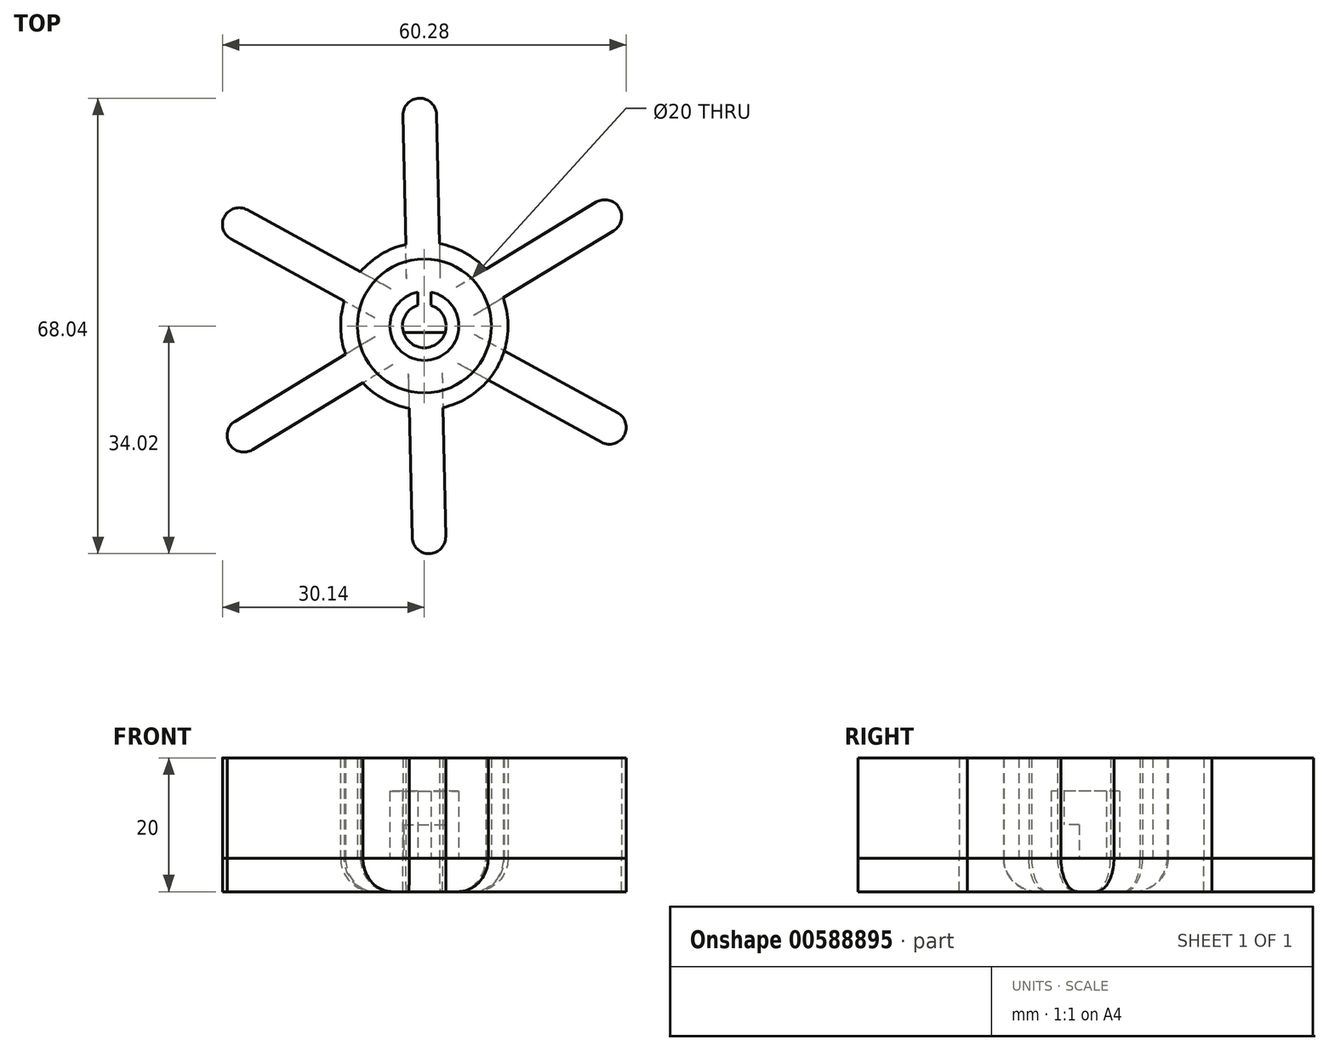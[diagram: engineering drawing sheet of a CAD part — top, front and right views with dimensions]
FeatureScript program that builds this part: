
annotation { "Feature Type Name" : "Feature", "Feature Type Description" : "" }
export const myFeature = defineFeature(function(context is Context, id is Id, definition is map)
    precondition{}
    {
        {
            var Q0;
            Q0=qCreatedBy(makeId("Top.planeOp"),FACE);
            var sketch = newSketch(context, id + "F0", { "sketchPlane" : qUnion([Q0])});
            skArc(sketch, "E0", {"start": v(-1, 3.1) * mm, "mid": v(0, -3.25) * mm, "end": v(1, 3.1) * mm});
            skArc(sketch, "E1", {"start": v(-1, 5.05) * mm, "mid": v(0, -5.15) * mm, "end": v(1, 5.05) * mm});
            skLineSegment(sketch, "E2", {"start": v(-1, 5.05) * mm, "end": v(-1, 3.1) * mm});
            skLineSegment(sketch, "E3", {"start": v(1, 5.05) * mm, "end": v(1, 3.1) * mm});
            skPoint(sketch, "E4.orphan", {"position": v(1, 6.28) * mm});
            skPoint(sketch, "E5.orphan", {"position": v(1, 2.2) * mm});
            skPoint(sketch, "E6.orphan", {"position": v(-1, 2.2) * mm});
            skPoint(sketch, "E7.orphan", {"position": v(-1, 6.28) * mm});
            skLineSegment(sketch, "E8", {"start": v(-3.1, -0.98) * mm, "end": v(3.1, -0.98) * mm});
            skCircle(sketch, "E9", {"center": v(0, 0) * mm, "radius": 10 * mm});
            skCircle(sketch, "E10", {"center": v(0, 0) * mm, "radius": 12.5 * mm});
            skLineSegment(sketch, "E11", {"start": v(11.94, -3.7) * mm, "end": v(28.84, -12.97) * mm});
            skLineSegment(sketch, "E12", {"start": v(29.83, -16.36) * mm, "end": v(29.83, -16.36) * mm});
            skLineSegment(sketch, "E13", {"start": v(26.44, -17.35) * mm, "end": v(9.54, -8.08) * mm});
            skPoint(sketch, "E14.visualSharp", {"position": v(31.03, -14.17) * mm});
            skArc(sketch, "E14.filletArc", {"start": v(29.83, -16.36) * mm, "mid": v(30.04, -14.46) * mm, "end": v(28.84, -12.97) * mm});
            skPoint(sketch, "E15.visualSharp", {"position": v(28.63, -18.56) * mm});
            skArc(sketch, "E15.filletArc", {"start": v(26.44, -17.35) * mm, "mid": v(28.34, -17.56) * mm, "end": v(29.83, -16.36) * mm});
            skLineSegment(sketch, "E16.1.0", {"start": v(9.17, 8.5) * mm, "end": v(25.65, 18.5) * mm});
            skLineSegment(sketch, "E16.1.1", {"start": v(28.25, 14.22) * mm, "end": v(11.77, 4.22) * mm});
            skArc(sketch, "E16.1.2", {"start": v(28.25, 14.22) * mm, "mid": v(29.38, 15.76) * mm, "end": v(29.09, 17.65) * mm});
            skArc(sketch, "E16.1.3", {"start": v(29.09, 17.65) * mm, "mid": v(27.54, 18.78) * mm, "end": v(25.65, 18.5) * mm});
            skLineSegment(sketch, "E16.2.0", {"start": v(-2.77, 12.19) * mm, "end": v(-3.19, 31.46) * mm});
            skLineSegment(sketch, "E16.2.1", {"start": v(1.81, 31.57) * mm, "end": v(2.23, 12.3) * mm});
            skArc(sketch, "E16.2.2", {"start": v(1.81, 31.57) * mm, "mid": v(1.04, 33.32) * mm, "end": v(-0.74, 34.02) * mm});
            skArc(sketch, "E16.2.3", {"start": v(-0.74, 34.02) * mm, "mid": v(-2.5, 33.25) * mm, "end": v(-3.19, 31.46) * mm});
            skLineSegment(sketch, "E16.3.0", {"start": v(-11.94, 3.7) * mm, "end": v(-28.84, 12.97) * mm});
            skLineSegment(sketch, "E16.3.1", {"start": v(-26.44, 17.35) * mm, "end": v(-9.54, 8.08) * mm});
            skArc(sketch, "E16.3.2", {"start": v(-26.44, 17.35) * mm, "mid": v(-28.34, 17.56) * mm, "end": v(-29.83, 16.36) * mm});
            skArc(sketch, "E16.3.3", {"start": v(-29.83, 16.36) * mm, "mid": v(-30.04, 14.46) * mm, "end": v(-28.84, 12.97) * mm});
            skLineSegment(sketch, "E16.4.0", {"start": v(-9.17, -8.5) * mm, "end": v(-25.65, -18.5) * mm});
            skLineSegment(sketch, "E16.4.1", {"start": v(-28.25, -14.22) * mm, "end": v(-11.77, -4.22) * mm});
            skArc(sketch, "E16.4.2", {"start": v(-28.25, -14.22) * mm, "mid": v(-29.38, -15.76) * mm, "end": v(-29.09, -17.65) * mm});
            skArc(sketch, "E16.4.3", {"start": v(-29.09, -17.65) * mm, "mid": v(-27.54, -18.78) * mm, "end": v(-25.65, -18.5) * mm});
            skLineSegment(sketch, "E16.5.0", {"start": v(2.77, -12.19) * mm, "end": v(3.19, -31.46) * mm});
            skLineSegment(sketch, "E16.5.1", {"start": v(-1.81, -31.57) * mm, "end": v(-2.23, -12.3) * mm});
            skArc(sketch, "E16.5.2", {"start": v(-1.81, -31.57) * mm, "mid": v(-1.04, -33.32) * mm, "end": v(0.74, -34.02) * mm});
            skArc(sketch, "E16.5.3", {"start": v(0.74, -34.02) * mm, "mid": v(2.5, -33.25) * mm, "end": v(3.19, -31.46) * mm});
            skSolve(sketch);
        }
        {
            var Q0;
            Q0=makeQuery(id+"F0.imprint","IMPRINT",FACE,{"disambiguationData":[TD([[makeQuery(id+"F0.imprint","IMPRINT",EDGE,{"derivedFrom":sQuery(id+"F0.wireOp",EDGE,"E1")}),1.0]])]});
            extrude(context, id + "F1", {"entities" : qUnion([Q0]), "depth" : 10 * mm, "offsetDistance" : 25 * mm});
        }
        {
            var Q0;
            {var subQ0=sQuery(id+"F0.wireOp",EDGE,"E8");Q0=makeQuery(id+"F0.imprint","IMPRINT",FACE,{"disambiguationData":[TD([[makeQuery(id+"F0.imprint","IMPRINT",EDGE,{"derivedFrom":subQ0}),-1.0]])]});}
            extrude(context, id + "F2", {"entities" : qUnion([Q0]), "operationType" : NewBodyOperationType.ADD, "depth" : 5 * mm, "offsetDistance" : 25 * mm});
        }
        {
            var Q0;
            Q0=makeQuery(id+"F0.imprint","IMPRINT",FACE,{"disambiguationData":[TD([[makeQuery(id+"F0.imprint","IMPRINT",EDGE,{"derivedFrom":sQuery(id+"F0.wireOp",EDGE,"E9")}),-1.0]])]});
            var Q1;
            {var subQ1=sQuery(id+"F0.wireOp",EDGE,"E16.1.0");Q1=makeQuery(id+"F0.imprint","IMPRINT",FACE,{"disambiguationData":[TD([[makeQuery(id+"F0.imprint","IMPRINT",EDGE,{"derivedFrom":subQ1}),-1.0]])]});}
            var Q2;
            {var subQ1=sQuery(id+"F0.wireOp",EDGE,"E16.2.0");Q2=makeQuery(id+"F0.imprint","IMPRINT",FACE,{"disambiguationData":[TD([[makeQuery(id+"F0.imprint","IMPRINT",EDGE,{"derivedFrom":subQ1}),-1.0]])]});}
            var Q3;
            {var subQ0=sQuery(id+"F0.wireOp",EDGE,"E16.3.0");Q3=makeQuery(id+"F0.imprint","IMPRINT",FACE,{"disambiguationData":[TD([[makeQuery(id+"F0.imprint","IMPRINT",EDGE,{"derivedFrom":subQ0}),-1.0]])]});}
            var Q4;
            {var subQ1=sQuery(id+"F0.wireOp",EDGE,"E16.4.0");Q4=makeQuery(id+"F0.imprint","IMPRINT",FACE,{"disambiguationData":[TD([[makeQuery(id+"F0.imprint","IMPRINT",EDGE,{"derivedFrom":subQ1}),-1.0]])]});}
            var Q5;
            {var subQ0=sQuery(id+"F0.wireOp",EDGE,"E16.5.0");Q5=makeQuery(id+"F0.imprint","IMPRINT",FACE,{"disambiguationData":[TD([[makeQuery(id+"F0.imprint","IMPRINT",EDGE,{"derivedFrom":subQ0}),-1.0]])]});}
            var Q6;
            {var subQ1=sQuery(id+"F0.wireOp",EDGE,"E11");Q6=makeQuery(id+"F0.imprint","IMPRINT",FACE,{"disambiguationData":[TD([[makeQuery(id+"F0.imprint","IMPRINT",EDGE,{"derivedFrom":subQ1}),-1.0]])]});}
            extrude(context, id + "F3", {"entities" : qUnion([Q0, Q1, Q2, Q3, Q4, Q5, Q6]), "depth" : 15 * mm, "offsetDistance" : 25 * mm});
        }
        {
            var Q0;
            Q0 = qSketchRegion(id + "F0", true);
            var Q1;
            Q1=makeQuery(id+"F0.imprint","IMPRINT",FACE,{"disambiguationData":[TD([[makeQuery(id+"F0.imprint","IMPRINT",EDGE,{"derivedFrom":sQuery(id+"F0.wireOp",EDGE,"E1")}),-1.0]])]});
            var Q2;
            {var subQ0=sQuery(id+"F0.wireOp",EDGE,"E8");Q2=makeQuery(id+"F0.imprint","IMPRINT",FACE,{"disambiguationData":[TD([[makeQuery(id+"F0.imprint","IMPRINT",EDGE,{"derivedFrom":subQ0}),-1.0]])]});}
            var Q3;
            Q3=makeQuery(id+"F0.imprint","IMPRINT",FACE,{"disambiguationData":[TD([[makeQuery(id+"F0.imprint","IMPRINT",EDGE,{"derivedFrom":sQuery(id+"F0.wireOp",EDGE,"E1")}),1.0]])]});
            extrude(context, id + "F4", {"entities" : qUnion([Q0, Q1, Q2, Q3]), "oppositeDirection" : true, "depth" : 5 * mm, "offsetDistance" : 25 * mm});
        }
        {
            var Q0;
            {var subQ1=sQuery(id+"F0.wireOp",EDGE,"E11");Q0=makeQuery(id+"F0.imprint","IMPRINT",FACE,{"disambiguationData":[TD([[makeQuery(id+"F0.imprint","IMPRINT",EDGE,{"derivedFrom":subQ1}),-1.0]])]});}
            extrude(context, id + "F5", {"entities" : qUnion([Q0]), "depth" : 15 * mm, "offsetDistance" : 25 * mm});
        }
        {
            var Q0;
            Q0=makeQuery(id+"F4.opExtrude","CAP_EDGE",EDGE,{"disambiguationData":[OSD([sQuery(id+"F0.wireOp",EDGE,"E10")])],"isStart":false});
            fillet(context, id + "F6", {"entities" : qUnion([Q0]), "radius" : 5 * mm, "tangentPropagation" : true, "allowEdgeOverflow" : false});
        }
    });
